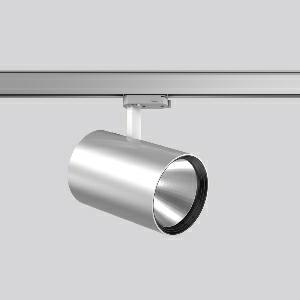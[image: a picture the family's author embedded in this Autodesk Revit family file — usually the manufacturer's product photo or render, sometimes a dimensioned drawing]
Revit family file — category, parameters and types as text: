
# Revit family: deecos_s_maxi_742220_004_76_a2c7
name_source: partatom
category: Lighting Fixtures
units: mm (PartAtom-declared; Revit-internal decimal feet)

## family parameters
Cut with Voids When Loaded = No
Host = Face
Light Source = No
Part Type = Normal
Room Calculation Point = No
Round Connector Dimension = Use Diameter
Shared = No

## types (1)
- DEECOS S maxi (1 x LED Modul 930, 4200 lm, 3000)
    Apparent Load = 35 VA
    Approval mark = CE
    CIE Flux Codes = 100 100 100 100 100
    Color Rendering = 90
    Color Temperature = 3000
    Default Elevation = 1800 mm
    Description = Series: DEECOS S maxi
LED surface-mounted projector in modern design with no visible cooling ribs. Housing: die-cast aluminium, powder-coated. Rotation range: 356°. Swivel range: 90°. Black plastic ring and recessed LED to prevent glare from the side. Optical assembly with reflector made of MIRO-Silver with 98% total light reflection for outstanding efficiency - can be changed without tools. Best colour rendering index Ra>90. With adapter for RZB 3-circuit DALI tracks. Suitable for Track on ceiling, Wall track. High quality converter without flickering and stroboscopic effect. The following accessories can be mounted without use of tools: interchangeable lenses, decorative glasses, honeycomb louvre, clear and frosted diffusers, white interchangeable plastic ring. 
Colour: silver
Diameter: 123 mm
Height: 200 mm
Lamp: LED
Socket: without socket
Colour temperature: 3000K
Colour rendering index (CRI): 92
System power: 35 W
Rated luminous flux: 4200 lm
Luminous efficiency: 120 lm/W
Control gear: Converter, dimmable, DALI
Protection class: I
Type of protection: IP 20
    Height = 200 mm  [stored 0.656168 ft]
    Lamp = 1 x LED Modul 930
    Lamp Light Flux = 4200 lm
    Lamp count = 1
    Length = 123 mm
    Lifetime = 50000 h
    Luminous efficacy = 120 lm/W
    Manufacturer = RZB
    ModVariant = No
    Model = 742220.004.76
    Mounting Place = Ceiling
    Mounting Type = Rail mounted
    Number of Poles = 1
    OnlyDefault = Yes
    Power Factor = 1
    Product Name = DEECOS S maxi
    Product group = Track mounted projectors
    ProductGroupID = 301
    Protection Class = Protection class I
    Protection Degree = IP 20
    RLX_Detail_Level = 1
    RLX_Emergency_Light_Flux = 0 lm
    RLX_Emergency_Type = 0
    RLX_Emergency_Type_DB = No
    RlxData = <blob elided: 40361 chars, md5=0bb713e1>
    Socket = socket
    Standby Power = 0 W
    System Light Flux = 4200 lm
    System Power = 35 W
    Type Comments = Product without accessories
    Type Image = 741954.004.jpg
    URL = http://relux.com
    VarID = ---
    Voltage = 230 V
    Voltage Range = 220-240 V
    Weight = 0.00 kg
    Width = 0 mm  [stored 0 ft]

note: [stored X ft] marks values corroborated as IEEE doubles in the binary element streams (Revit-internal decimal feet)

## geometry (parser evidence)
native form markers: Blend x4, Sweep x10
no freeform markers — native parametric forms only
